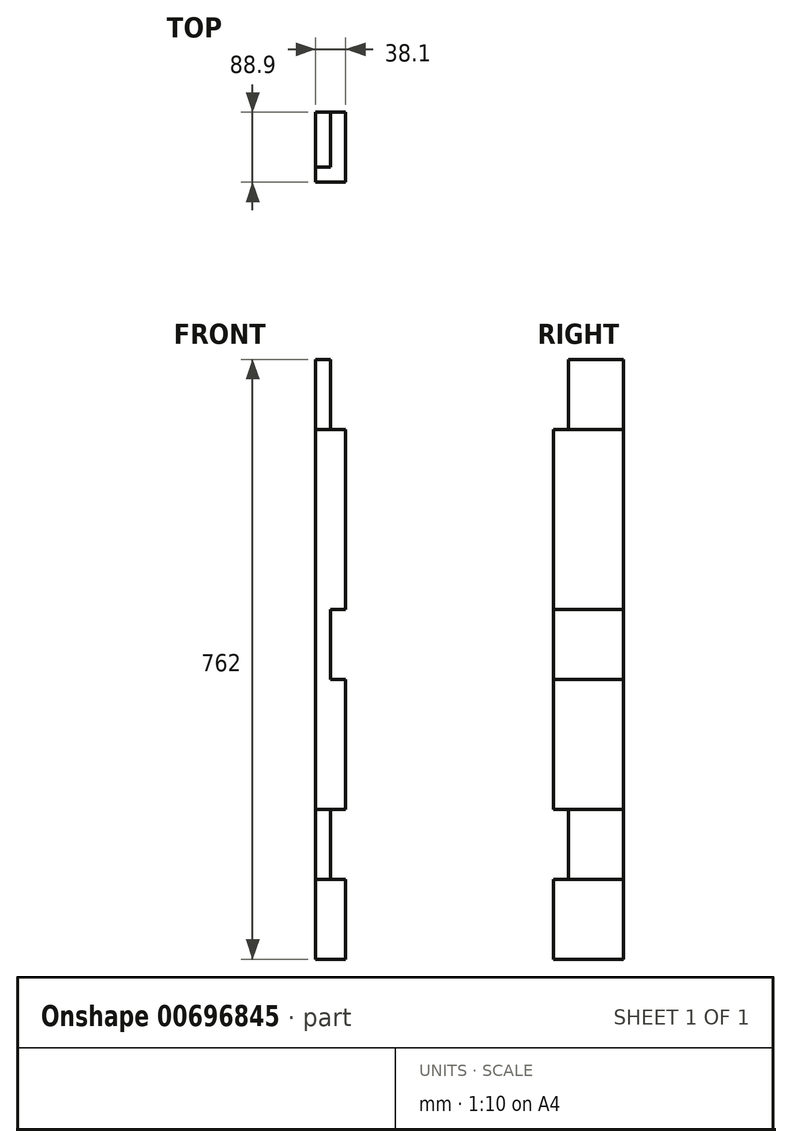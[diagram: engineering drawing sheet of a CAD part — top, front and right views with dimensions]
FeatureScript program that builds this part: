
annotation { "Feature Type Name" : "Feature", "Feature Type Description" : "" }
export const myFeature = defineFeature(function(context is Context, id is Id, definition is map)
    precondition{}
    {
        {
            var Q0;
            Q0=qCreatedBy(makeId("Top.planeOp"),FACE);
            var sketch = newSketch(context, id + "F0", { "sketchPlane" : qUnion([Q0])});
            skLineSegment(sketch, "E0.bottom", {"start": v(0, 0) * mm, "end": v(38.1, 0) * mm});
            skLineSegment(sketch, "E0.top", {"start": v(0, 88.9) * mm, "end": v(38.1, 88.9) * mm});
            skLineSegment(sketch, "E0.left", {"start": v(0, 0) * mm, "end": v(0, 88.9) * mm});
            skLineSegment(sketch, "E0.right", {"start": v(38.1, 0) * mm, "end": v(38.1, 88.9) * mm});
            skSolve(sketch);
        }
        {
            var Q0;
            Q0=qSketchRegion(id+"F0",true);
            extrude(context, id + "F1", {"entities" : qUnion([Q0]), "depth" : 762 * mm, "offsetDistance" : 25.4 * mm});
        }
        {
            var Q0;
            Q0=makeQuery(id+"F1.opExtrude","SWEPT_FACE",FACE,{"disambiguationData":[OSD([sQuery(id+"F0.wireOp",EDGE,"E0.bottom")])]});
            var sketch = newSketch(context, id + "F2", { "sketchPlane" : qUnion([Q0])});
            skLineSegment(sketch, "E1.bottom", {"start": v(38.1, 762) * mm, "end": v(19.05, 762) * mm});
            skLineSegment(sketch, "E1.top", {"start": v(38.1, 673.1) * mm, "end": v(19.05, 673.1) * mm});
            skLineSegment(sketch, "E1.left", {"start": v(38.1, 762) * mm, "end": v(38.1, 673.1) * mm});
            skLineSegment(sketch, "E1.right", {"start": v(19.05, 762) * mm, "end": v(19.05, 673.1) * mm});
            skSolve(sketch);
        }
        {
            var Q0;
            Q0 = qSketchRegion(id + "F2", true);
            extrude(context, id + "F3", {"entities" : qUnion([Q0]), "operationType" : NewBodyOperationType.REMOVE, "endBound" : BoundingType.THROUGH_ALL, "oppositeDirection" : true, "depth" : 25.4 * mm, "offsetDistance" : 25.4 * mm});
        }
        {
            var Q0;
            Q0=makeQuery(id+"F1.opExtrude","SWEPT_FACE",FACE,{"disambiguationData":[OSD([sQuery(id+"F0.wireOp",EDGE,"E0.bottom")])]});
            var sketch = newSketch(context, id + "F4", { "sketchPlane" : qUnion([Q0])});
            skLineSegment(sketch, "E2.bottom", {"start": v(38.1, 190.5) * mm, "end": v(19.05, 190.5) * mm});
            skLineSegment(sketch, "E2.top", {"start": v(38.1, 101.6) * mm, "end": v(19.05, 101.6) * mm});
            skLineSegment(sketch, "E2.left", {"start": v(38.1, 190.5) * mm, "end": v(38.1, 101.6) * mm});
            skLineSegment(sketch, "E2.right", {"start": v(19.05, 190.5) * mm, "end": v(19.05, 101.6) * mm});
            skSolve(sketch);
        }
        {
            var Q0;
            Q0 = qSketchRegion(id + "F4", true);
            extrude(context, id + "F5", {"entities" : qUnion([Q0]), "operationType" : NewBodyOperationType.REMOVE, "endBound" : BoundingType.THROUGH_ALL, "oppositeDirection" : true, "depth" : 25.4 * mm, "offsetDistance" : 25.4 * mm});
        }
        {
            var Q0;
            Q0=makeQuery(id+"F1.opExtrude","SWEPT_FACE",FACE,{"disambiguationData":[OSD([sQuery(id+"F0.wireOp",EDGE,"E0.bottom")])]});
            var sketch = newSketch(context, id + "F6", { "sketchPlane" : qUnion([Q0])});
            skLineSegment(sketch, "E3.bottom", {"start": v(38.1, 444.5) * mm, "end": v(19.05, 444.5) * mm});
            skLineSegment(sketch, "E3.top", {"start": v(38.1, 355.6) * mm, "end": v(19.05, 355.6) * mm});
            skLineSegment(sketch, "E3.left", {"start": v(38.1, 444.5) * mm, "end": v(38.1, 355.6) * mm});
            skLineSegment(sketch, "E3.right", {"start": v(19.05, 444.5) * mm, "end": v(19.05, 355.6) * mm});
            skSolve(sketch);
        }
        {
            var Q0;
            Q0 = qSketchRegion(id + "F6", true);
            extrude(context, id + "F7", {"entities" : qUnion([Q0]), "operationType" : NewBodyOperationType.REMOVE, "endBound" : BoundingType.THROUGH_ALL, "oppositeDirection" : true, "depth" : 25.4 * mm, "offsetDistance" : 25.4 * mm});
        }
        {
            var Q0;
            Q0=makeQuery(id+"F5.boolean.opBoolean","COPY",FACE,{"derivedFrom":makeQuery(id+"F5.opExtrude","SWEPT_FACE",FACE,{"disambiguationData":[OSD([sQuery(id+"F4.wireOp",EDGE,"E2.right")])]})});
            var sketch = newSketch(context, id + "F8", { "sketchPlane" : qUnion([Q0])});
            skLineSegment(sketch, "E4.bottom", {"start": v(0, 190.5) * mm, "end": v(19.05, 190.5) * mm});
            skLineSegment(sketch, "E4.top", {"start": v(0, 101.6) * mm, "end": v(19.05, 101.6) * mm});
            skLineSegment(sketch, "E4.left", {"start": v(0, 190.5) * mm, "end": v(0, 101.6) * mm});
            skLineSegment(sketch, "E4.right", {"start": v(19.05, 190.5) * mm, "end": v(19.05, 101.6) * mm});
            skSolve(sketch);
        }
        {
            var Q0;
            Q0 = qSketchRegion(id + "F8", true);
            extrude(context, id + "F9", {"entities" : qUnion([Q0]), "operationType" : NewBodyOperationType.REMOVE, "endBound" : BoundingType.THROUGH_ALL, "oppositeDirection" : true, "depth" : 25.4 * mm, "offsetDistance" : 25.4 * mm});
        }
        {
            var Q0;
            Q0=makeQuery(id+"F3.boolean.opBoolean","COPY",FACE,{"derivedFrom":makeQuery(id+"F3.opExtrude","SWEPT_FACE",FACE,{"disambiguationData":[OSD([sQuery(id+"F2.wireOp",EDGE,"E1.right")])]})});
            var sketch = newSketch(context, id + "F10", { "sketchPlane" : qUnion([Q0])});
            skLineSegment(sketch, "E5.bottom", {"start": v(0, 673.1) * mm, "end": v(19.05, 673.1) * mm});
            skLineSegment(sketch, "E5.top", {"start": v(0, 762) * mm, "end": v(19.05, 762) * mm});
            skLineSegment(sketch, "E5.left", {"start": v(0, 673.1) * mm, "end": v(0, 762) * mm});
            skLineSegment(sketch, "E5.right", {"start": v(19.05, 673.1) * mm, "end": v(19.05, 762) * mm});
            skSolve(sketch);
        }
        {
            var Q0;
            Q0 = qSketchRegion(id + "F10", true);
            extrude(context, id + "F11", {"entities" : qUnion([Q0]), "operationType" : NewBodyOperationType.REMOVE, "endBound" : BoundingType.THROUGH_ALL, "oppositeDirection" : true, "depth" : 25.4 * mm, "offsetDistance" : 25.4 * mm});
        }
    });
